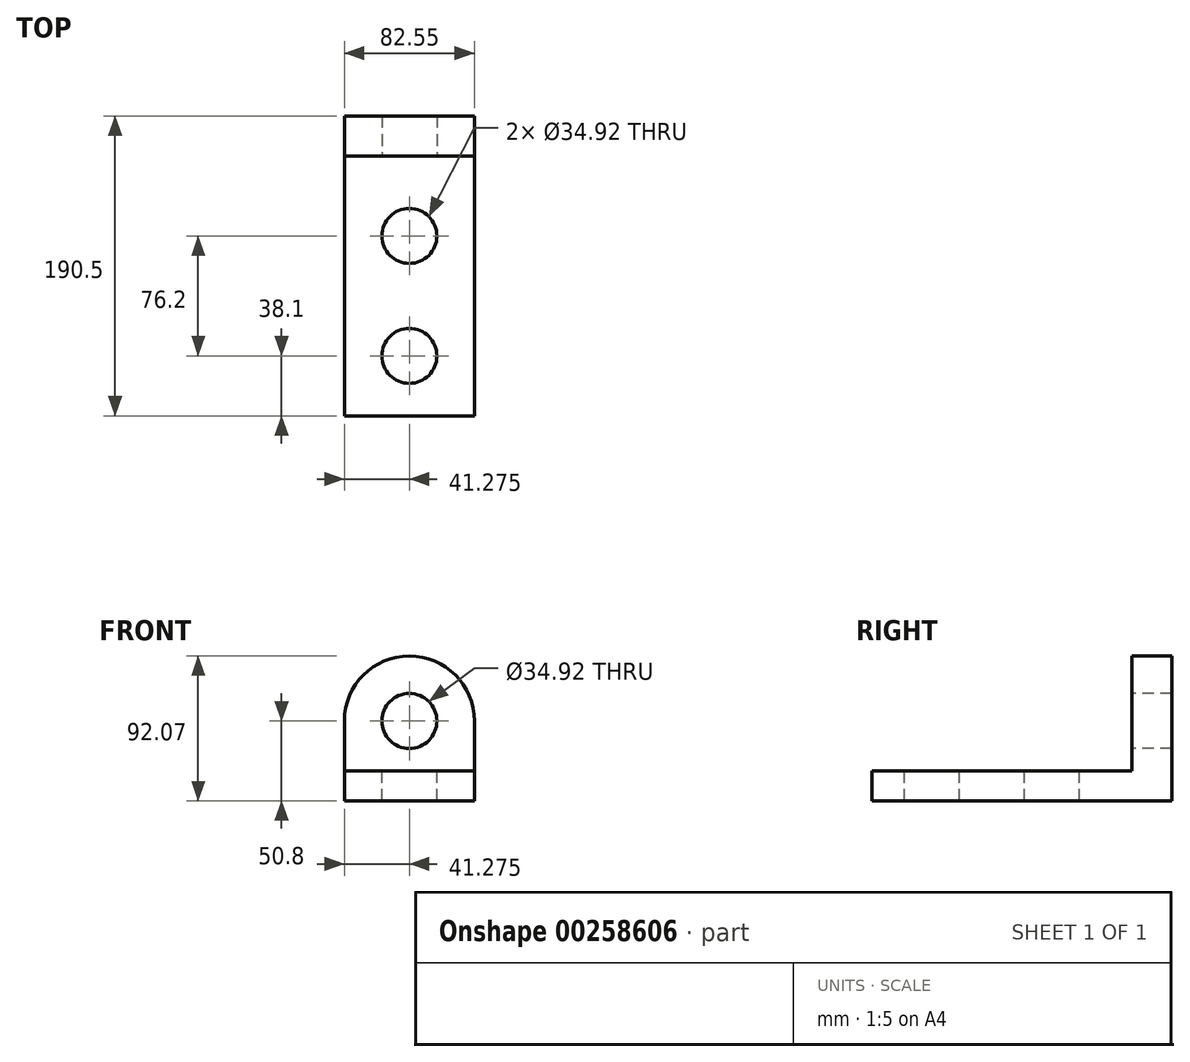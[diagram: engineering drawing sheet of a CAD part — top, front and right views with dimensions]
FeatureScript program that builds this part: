
annotation { "Feature Type Name" : "Feature", "Feature Type Description" : "" }
export const myFeature = defineFeature(function(context is Context, id is Id, definition is map)
    precondition{}
    {
        {
            var Q0;
            Q0=qCreatedBy(makeId("Top.planeOp"),FACE);
            var sketch = newSketch(context, id + "F0", { "sketchPlane" : qUnion([Q0])});
            skLineSegment(sketch, "E0.bottom", {"start": v(0, 0) * mm, "end": v(82.55, 0) * mm});
            skLineSegment(sketch, "E0.top", {"start": v(0, 190.5) * mm, "end": v(82.55, 190.5) * mm});
            skLineSegment(sketch, "E0.left", {"start": v(0, 0) * mm, "end": v(0, 190.5) * mm});
            skLineSegment(sketch, "E0.right", {"start": v(82.55, 0) * mm, "end": v(82.55, 190.5) * mm});
            skSolve(sketch);
        }
        {
            var Q0;
            Q0=makeQuery(id+"F0.imprint","IMPRINT",FACE,{"disambiguationData":[TD([[makeQuery(id+"F0.imprint","IMPRINT",EDGE,{"derivedFrom":sQuery(id+"F0.wireOp",EDGE,"E0.bottom")}),1.0]])]});
            extrude(context, id + "F1", {"entities" : qUnion([Q0]), "depth" : 19.05 * mm});
        }
        {
            var Q0;
            Q0=makeQuery(id+"F1.opExtrude","CAP_FACE",FACE,{"disambiguationData":[OSD([sQuery(id+"F0.wireOp",EDGE,"E0.bottom"),sQuery(id+"F0.wireOp",EDGE,"E0.top"),sQuery(id+"F0.wireOp",EDGE,"E0.left"),sQuery(id+"F0.wireOp",EDGE,"E0.right")])],"isStart":false});
            var sketch = newSketch(context, id + "F2", { "sketchPlane" : qUnion([Q0])});
            skLineSegment(sketch, "E1.bottom", {"start": v(0, 190.5) * mm, "end": v(82.55, 190.5) * mm});
            skLineSegment(sketch, "E1.top", {"start": v(0, 165.1) * mm, "end": v(82.55, 165.1) * mm});
            skLineSegment(sketch, "E1.left", {"start": v(0, 190.5) * mm, "end": v(0, 165.1) * mm});
            skLineSegment(sketch, "E1.right", {"start": v(82.55, 190.5) * mm, "end": v(82.55, 165.1) * mm});
            skSolve(sketch);
        }
        {
            var Q0;
            Q0=makeQuery(id+"F2.imprint","IMPRINT",FACE,{"disambiguationData":[TD([[makeQuery(id+"F2.imprint","IMPRINT",EDGE,{"derivedFrom":sQuery(id+"F2.wireOp",EDGE,"E1.bottom")}),-1.0]])]});
            extrude(context, id + "F3", {"entities" : qUnion([Q0]), "operationType" : NewBodyOperationType.ADD, "depth" : 73.02 * mm});
        }
        {
            var Q0;
            Q0=makeQuery(id+"F3.opExtrude","CAP_EDGE",EDGE,{"disambiguationData":[OSD([sQuery(id+"F2.wireOp",EDGE,"E1.left")])],"isStart":false});
            var Q1;
            Q1=makeQuery(id+"F3.opExtrude","CAP_EDGE",EDGE,{"disambiguationData":[OSD([sQuery(id+"F2.wireOp",EDGE,"E1.right")])],"isStart":false});
            fillet(context, id + "F4", {"entities" : qUnion([Q0, Q1]), "radius" : 41.27 * mm, "tangentPropagation" : true, "allowEdgeOverflow" : false});
        }
        {
            var Q0;
            Q0=makeQuery(id+"F3.opExtrude","SWEPT_FACE",FACE,{"disambiguationData":[OSD([sQuery(id+"F2.wireOp",EDGE,"E1.top")])]});
            var sketch = newSketch(context, id + "F5", { "sketchPlane" : qUnion([Q0])});
            skCircle(sketch, "E2", {"center": v(41.27, 50.8) * mm, "radius": 17.46 * mm});
            skSolve(sketch);
        }
        {
            var Q0;
            Q0=makeQuery(id+"F5.imprint","IMPRINT",FACE,{"disambiguationData":[TD([[makeQuery(id+"F5.imprint","IMPRINT",EDGE,{"derivedFrom":sQuery(id+"F5.wireOp",EDGE,"E2")}),1.0]])]});
            extrude(context, id + "F6", {"entities" : qUnion([Q0]), "operationType" : NewBodyOperationType.REMOVE, "oppositeDirection" : true, "depth" : 25.4 * mm});
        }
        {
            var Q0;
            Q0=makeQuery(id+"F1.opExtrude","CAP_FACE",FACE,{"disambiguationData":[OSD([sQuery(id+"F0.wireOp",EDGE,"E0.bottom"),sQuery(id+"F0.wireOp",EDGE,"E0.top"),sQuery(id+"F0.wireOp",EDGE,"E0.left"),sQuery(id+"F0.wireOp",EDGE,"E0.right")])],"isStart":false});
            var sketch = newSketch(context, id + "F7", { "sketchPlane" : qUnion([Q0])});
            skLineSegment(sketch, "E3", {"start": v(41.28, 0) * mm, "end": v(41.28, 38.1) * mm});
            skCircle(sketch, "E4", {"center": v(41.28, 38.1) * mm, "radius": 17.46 * mm});
            skLineSegment(sketch, "E5", {"start": v(41.28, 38.1) * mm, "end": v(41.28, 114.3) * mm});
            skCircle(sketch, "E6", {"center": v(41.28, 114.3) * mm, "radius": 17.46 * mm});
            skSolve(sketch);
        }
        {
            var Q0;
            Q0=makeQuery(id+"F7.imprint","IMPRINT",FACE,{"disambiguationData":[TD([[makeQuery(id+"F7.imprint","IMPRINT",EDGE,{"derivedFrom":sQuery(id+"F7.wireOp",EDGE,"E6")}),1.0]])]});
            var Q1;
            {var subQ0=sQuery(id+"F7.wireOp",EDGE,"E5");var subQ1=sQuery(id+"F7.wireOp",EDGE,"E3");var subQ2=makeQuery(id+"F7.imprint","INTERSECT",VERTEX,{"derivedFrom":[subQ1,subQ0]});Q1=makeQuery(id+"F7.imprint","IMPRINT",FACE,{"disambiguationData":[TD([[makeQuery(id+"F7.imprint","IMPRINT",EDGE,{"disambiguationData":[TD([[subQ2,1.0]])],"derivedFrom":subQ1}),-1.0]])]});}
            var Q2;
            {var subQ0=sQuery(id+"F7.wireOp",EDGE,"E5");var subQ1=sQuery(id+"F7.wireOp",EDGE,"E3");var subQ2=makeQuery(id+"F7.imprint","INTERSECT",VERTEX,{"derivedFrom":[subQ1,subQ0]});Q2=makeQuery(id+"F7.imprint","IMPRINT",FACE,{"disambiguationData":[TD([[makeQuery(id+"F7.imprint","IMPRINT",EDGE,{"disambiguationData":[TD([[subQ2,1.0]])],"derivedFrom":subQ1}),1.0]])]});}
            extrude(context, id + "F8", {"entities" : qUnion([Q0, Q1, Q2]), "operationType" : NewBodyOperationType.REMOVE, "oppositeDirection" : true, "depth" : 25.4 * mm});
        }
    });
